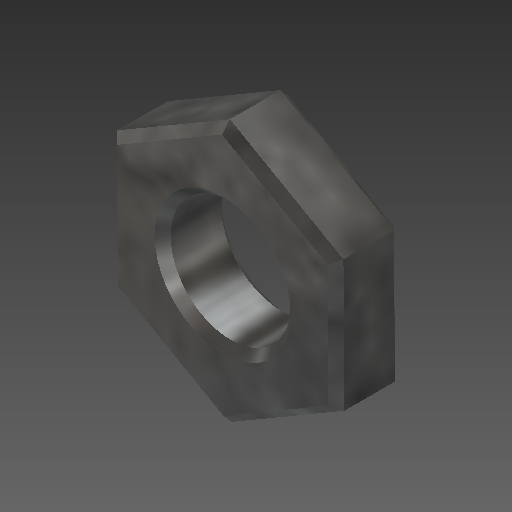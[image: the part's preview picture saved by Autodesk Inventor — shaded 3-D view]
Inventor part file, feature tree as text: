
AUTODESK INVENTOR PART (.ipt)
format: ipt  version: 2018 (Build 220112000, 112)  size: 159,744 bytes
history: native  units: mm
features: extrude x1, chamfer x1, sketch x1
ambient origin geometry x8: Origin, YZ Plane, XZ Plane, XY Plane, X Axis, Y Axis, Z Axis, Center Point
bodies: Solid1 (feature_tree)
feature tree (3):
  extrude  "Extrusion1"  Depth=5.0mm
  chamfer  "Chamfer1"  Distance=5.0mm
  sketch  "Sketch1"  dims[d0=9.02mm d1=8.5mm d2=5.0mm d3=0.0mm d4=0.6mm d5=2.0mm d6=45.0deg]
